# Revit family: Hager-GOLF-Flush_mounted-IP40-With_Cover-With_DIN-NoHosted-ES-es
name_source: partatom
category: Electrical Equipment
units: mm (PartAtom-declared; Revit-internal decimal feet)

## family parameters
Always vertical = Yes
Cut with Voids When Loaded = No
Maintain Annotation Orientation = No
Panel Configuration = Two Columns, Circuits Across
Part Type = Panelboard
Room Calculation Point = No
Round Connector Dimension = Use Diameter
Shared = No
Work Plane-Based = Yes

## types (69) — shared parameters
Code hager = ADD-EC000214_EU
Default Elevation = 1200 mm
EF000003 - Método de montaje = Montado empotrado (escayola)
EF000007 - Color = Blanco
EF000024 - Resistente a UV = No
EF000049 - Profundidad = 97 mm  [stored 0.318241 ft]
EF000116 - Número RAL = 9010
EF000118 - Con placa de montaje = No
EF000218 - Profundidad de instalación = 72 mm  [stored 0.23622 ft]
EF001062 - Versión de CEM = No
EF001134 - Carril DIN = Yes
EF004462 - Tipo de cierre = Otros
EF005474 - Grado de protección (IP) = IP40
EF006306 - Con candado = No
EF009212 - Versión de la cubierta = Cerrado
ETIM class code = EC000214
ETIM class name = Small distribution board
HG000001 - Número de columnas = 1
HG000002-with door or cover-es = Yes
HG000003-Range-es = GOLF
HG000005-Thickness-es = 2 mm  [stored 0.00656168 ft]
HG000006-Flush mounted-es = Yes
HG000009-Double swing door-es = No
HG000010-Asymmetric doors-es = No
HG000011-Empty rows from bottom-es = No
HG000012-Door swing angle-es = 90.00°
HG000013-Door on the left-es = No
HG000014-Door on the right-es = Yes
HG000015-Clearance visibility-es = Yes
HG000016-Door 3D visibility-es = Yes
HG000017-Distance between poles-es = 18 mm  [stored 0.0590551 ft]
HG000060-RAL-number = 9010
HG000099-Onfly Template ID-es-ES = 507532
Manufacturer = Hager
Name BIM&CO = Electricity
Name hager = ADD_Enclosures_EC000214
Reference = Template-Enclosure_EU-EC000214
Uniformat = Low Tension Service & Dist.
Uniformat code = D501001
zero-valued in all types: EF001131 - Profundidad interna, HG000007-Number of empty columns-es, HG000008-Number of empty rows-es

## per-type parameters (varying)
| type | BC_METADATA | EF000008 - Anchura | EF000040 - Altura | EF000266 - Número de filas | EF000332 - Altura de la instalación | EF000846 - Anchura de montaje | EF001088 - Posibilidad de extensión | EF002950 - Ancho en número de espacios modulares | EF006244 - Tapa/puerta transparente | EF015776 - Borne de tierra | EF015777 - Borne neutro | EF015941 - Puerta de transmisión de señal | HG000004-Manufacturer reference-es | HGEF000266-Número de filas | HGEF0002950-Ancho en número de espacios modulares |
| GOLF-Flush_mounted_W204_H225_D97_4_Modular_Spacing-VF104PE | {"ObjectGuid":"21a461f2-d2cc-43be-887c-1bcd842bd4ee","ModelGuid":"3472f7aa-0217-42d1-acd3-302686f3a51c","VariantGuid":"67abac47-0447-4a06-9074-36f65eb0749b","Revision":"#5","VariantName":"GOLF-Flush_mounted_W204_H225_D97_4_Modular_Spacing-VF104PE"} | 204 mm | 225 mm  [stored 0.738189 ft] | 1 | 189 mm  [stored 0.620079 ft] | 170 mm  [stored 0.557743 ft] | Yes | 4 | No | Yes | No | Yes | VF104PE | 1 | 4 |
| GOLF-Flush_mounted_W204_H225_D97_4_Modular_Spacing-VF104PEH | {"ObjectGuid":"21a461f2-d2cc-43be-887c-1bcd842bd4ee","ModelGuid":"3472f7aa-0217-42d1-acd3-302686f3a51c","VariantGuid":"bf5ffc28-fc6f-4c9d-8d83-cb40cf3ecd5b","Revision":"#5","VariantName":"GOLF-Flush_mounted_W204_H225_D97_4_Modular_Spacing-VF104PEH"} | 204 mm | 225 mm  [stored 0.738189 ft] | 1 | 189 mm  [stored 0.620079 ft] | 170 mm  [stored 0.557743 ft] | Yes | 4 | No | Yes | No | Yes | VF104PEH | 1 | 4 |
| GOLF-Flush_mounted_W204_H225_D97_4_Modular_Spacing-VF104TE | {"ObjectGuid":"21a461f2-d2cc-43be-887c-1bcd842bd4ee","ModelGuid":"3472f7aa-0217-42d1-acd3-302686f3a51c","VariantGuid":"7042e25b-f324-46a0-bf15-9dd9586686e8","Revision":"#5","VariantName":"GOLF-Flush_mounted_W204_H225_D97_4_Modular_Spacing-VF104TE"} | 204 mm | 225 mm  [stored 0.738189 ft] | 1 | 189 mm  [stored 0.620079 ft] | 170 mm  [stored 0.557743 ft] | Yes | 4 | Yes | Yes | No | Yes | VF104TE | 1 | 4 |
| GOLF-Flush_mounted_W275_H225_D97_8_Modular_Spacing-VF108PE | {"ObjectGuid":"21a461f2-d2cc-43be-887c-1bcd842bd4ee","ModelGuid":"3472f7aa-0217-42d1-acd3-302686f3a51c","VariantGuid":"06116414-54d7-4273-82dc-95a411ece082","Revision":"#5","VariantName":"GOLF-Flush_mounted_W275_H225_D97_8_Modular_Spacing-VF108PE"} | 275 mm | 225 mm  [stored 0.738189 ft] | 1 | 189 mm  [stored 0.620079 ft] | 242 mm  [stored 0.793963 ft] | Yes | 8 | No | Yes | No | Yes | VF108PE | 1 | 8 |
| GOLF-Flush_mounted_W275_H225_D97_8_Modular_Spacing-VF108PEH | {"ObjectGuid":"21a461f2-d2cc-43be-887c-1bcd842bd4ee","ModelGuid":"3472f7aa-0217-42d1-acd3-302686f3a51c","VariantGuid":"36ce2ec1-e60a-4bf2-a514-3e6662372eb3","Revision":"#5","VariantName":"GOLF-Flush_mounted_W275_H225_D97_8_Modular_Spacing-VF108PEH"} | 275 mm | 225 mm  [stored 0.738189 ft] | 1 | 189 mm  [stored 0.620079 ft] | 242 mm  [stored 0.793963 ft] | Yes | 8 | No | Yes | No | Yes | VF108PEH | 1 | 8 |
| GOLF-Flush_mounted_W275_H225_D97_8_Modular_Spacing-VF108TE | {"ObjectGuid":"21a461f2-d2cc-43be-887c-1bcd842bd4ee","ModelGuid":"3472f7aa-0217-42d1-acd3-302686f3a51c","VariantGuid":"5955d0a4-5d32-445a-b466-02b6bf6b212f","Revision":"#5","VariantName":"GOLF-Flush_mounted_W275_H225_D97_8_Modular_Spacing-VF108TE"} | 275 mm | 225 mm  [stored 0.738189 ft] | 1 | 189 mm  [stored 0.620079 ft] | 242 mm  [stored 0.793963 ft] | Yes | 8 | Yes | Yes | No | Yes | VF108TE | 1 | 8 |
| GOLF-Flush_mounted_W275_H225_D97_8_Modular_Spacing-VF108TJ | {"ObjectGuid":"21a461f2-d2cc-43be-887c-1bcd842bd4ee","ModelGuid":"3472f7aa-0217-42d1-acd3-302686f3a51c","VariantGuid":"db803c6c-c584-49ad-b8cc-c973fc13c8e5","Revision":"#5","VariantName":"GOLF-Flush_mounted_W275_H225_D97_8_Modular_Spacing-VF108TJ"} | 275 mm | 225 mm  [stored 0.738189 ft] | 1 | 189 mm  [stored 0.620079 ft] | 242 mm  [stored 0.793963 ft] | Yes | 8 | Yes | Yes | Yes | Yes | VF108TJ | 1 | 8 |
| GOLF-Flush_mounted_W352_H293_D97_12_Modular_Spacing-VF112PE | {"ObjectGuid":"21a461f2-d2cc-43be-887c-1bcd842bd4ee","ModelGuid":"3472f7aa-0217-42d1-acd3-302686f3a51c","VariantGuid":"c39431f9-d04a-4a2b-91f6-57de3b093784","Revision":"#5","VariantName":"GOLF-Flush_mounted_W352_H293_D97_12_Modular_Spacing-VF112PE"} | 352 mm  [stored 1.15486 ft] | 293 mm | 1 | 257 mm  [stored 0.843176 ft] | 318 mm  [stored 1.04331 ft] | Yes | 12 | No | Yes | No | Yes | VF112PE | 1 | 12 |
| GOLF-Flush_mounted_W352_H293_D97_12_Modular_Spacing-VF112PEH | {"ObjectGuid":"21a461f2-d2cc-43be-887c-1bcd842bd4ee","ModelGuid":"3472f7aa-0217-42d1-acd3-302686f3a51c","VariantGuid":"8f0d8f87-0006-4b11-8d38-30c6d8bf758f","Revision":"#5","VariantName":"GOLF-Flush_mounted_W352_H293_D97_12_Modular_Spacing-VF112PEH"} | 352 mm  [stored 1.15486 ft] | 293 mm | 1 | 257 mm  [stored 0.843176 ft] | 318 mm  [stored 1.04331 ft] | Yes | 12 | No | Yes | No | Yes | VF112PEH | 1 | 12 |
| GOLF-Flush_mounted_W352_H293_D97_12_Modular_Spacing-VF112PJ | {"ObjectGuid":"21a461f2-d2cc-43be-887c-1bcd842bd4ee","ModelGuid":"3472f7aa-0217-42d1-acd3-302686f3a51c","VariantGuid":"0c9c232a-2e7f-4892-bcb4-da88733a4bf1","Revision":"#5","VariantName":"GOLF-Flush_mounted_W352_H293_D97_12_Modular_Spacing-VF112PJ"} | 352 mm  [stored 1.15486 ft] | 293 mm | 1 | 257 mm  [stored 0.843176 ft] | 318 mm  [stored 1.04331 ft] | Yes | 12 | No | Yes | Yes | Yes | VF112PJ | 1 | 12 |
| GOLF-Flush_mounted_W352_H293_D97_12_Modular_Spacing-VF112PY | {"ObjectGuid":"21a461f2-d2cc-43be-887c-1bcd842bd4ee","ModelGuid":"3472f7aa-0217-42d1-acd3-302686f3a51c","VariantGuid":"afb2a40a-fb85-4b57-bab9-55e2ace79b82","Revision":"#5","VariantName":"GOLF-Flush_mounted_W352_H293_D97_12_Modular_Spacing-VF112PY"} | 352 mm  [stored 1.15486 ft] | 293 mm | 1 | 257 mm  [stored 0.843176 ft] | 318 mm  [stored 1.04331 ft] | Yes | 12 | No | No | No | No | VF112PY | 1 | 12 |
| GOLF-Flush_mounted_W352_H293_D97_12_Modular_Spacing-VF112TE | {"ObjectGuid":"21a461f2-d2cc-43be-887c-1bcd842bd4ee","ModelGuid":"3472f7aa-0217-42d1-acd3-302686f3a51c","VariantGuid":"56dcd90f-e5ad-4723-8c6c-981950e4aafb","Revision":"#5","VariantName":"GOLF-Flush_mounted_W352_H293_D97_12_Modular_Spacing-VF112TE"} | 352 mm  [stored 1.15486 ft] | 293 mm | 1 | 257 mm  [stored 0.843176 ft] | 318 mm  [stored 1.04331 ft] | Yes | 12 | Yes | Yes | No | Yes | VF112TE | 1 | 12 |
| GOLF-Flush_mounted_W352_H293_D97_12_Modular_Spacing-VF112TF | {"ObjectGuid":"21a461f2-d2cc-43be-887c-1bcd842bd4ee","ModelGuid":"3472f7aa-0217-42d1-acd3-302686f3a51c","VariantGuid":"18a8c72d-3909-411f-af7f-3ef0debf2d79","Revision":"#5","VariantName":"GOLF-Flush_mounted_W352_H293_D97_12_Modular_Spacing-VF112TF"} | 352 mm  [stored 1.15486 ft] | 293 mm | 1 | 257 mm  [stored 0.843176 ft] | 318 mm  [stored 1.04331 ft] | Yes | 12 | Yes | Yes | No | Yes | VF112TF | 1 | 12 |
| GOLF-Flush_mounted_W352_H293_D97_12_Modular_Spacing-VF112TJ | {"ObjectGuid":"21a461f2-d2cc-43be-887c-1bcd842bd4ee","ModelGuid":"3472f7aa-0217-42d1-acd3-302686f3a51c","VariantGuid":"e8fe70cc-cd10-46dc-9450-fec8598aad3c","Revision":"#5","VariantName":"GOLF-Flush_mounted_W352_H293_D97_12_Modular_Spacing-VF112TJ"} | 352 mm  [stored 1.15486 ft] | 293 mm | 1 | 257 mm  [stored 0.843176 ft] | 318 mm  [stored 1.04331 ft] | Yes | 12 | Yes | Yes | Yes | Yes | VF112TJ | 1 | 12 |
| GOLF-Flush_mounted_W352_H293_D97_12_Modular_Spacing-VF112TY | {"ObjectGuid":"21a461f2-d2cc-43be-887c-1bcd842bd4ee","ModelGuid":"3472f7aa-0217-42d1-acd3-302686f3a51c","VariantGuid":"f1fc716c-5d21-43a4-b735-6e5759e6688c","Revision":"#5","VariantName":"GOLF-Flush_mounted_W352_H293_D97_12_Modular_Spacing-VF112TY"} | 352 mm  [stored 1.15486 ft] | 293 mm | 1 | 257 mm  [stored 0.843176 ft] | 318 mm  [stored 1.04331 ft] | Yes | 12 | Yes | Yes | Yes | Yes | VF112TY | 1 | 12 |
| GOLF-Flush_mounted_W460_H293_D97_18_Modular_Spacing-VF118PEH | {"ObjectGuid":"21a461f2-d2cc-43be-887c-1bcd842bd4ee","ModelGuid":"3472f7aa-0217-42d1-acd3-302686f3a51c","VariantGuid":"ae20f4c4-2976-4c92-9248-da306b9a1619","Revision":"#5","VariantName":"GOLF-Flush_mounted_W460_H293_D97_18_Modular_Spacing-VF118PEH"} | 460 mm  [stored 1.50919 ft] | 293 mm | 1 | 257 mm  [stored 0.843176 ft] | 426 mm  [stored 1.39764 ft] | Yes | 18 | No | Yes | No | Yes | VF118PEH | 1 | 18 |
| GOLF-Flush_mounted_W460_H293_D97_18_Modular_Spacing-VF118PES | {"ObjectGuid":"21a461f2-d2cc-43be-887c-1bcd842bd4ee","ModelGuid":"3472f7aa-0217-42d1-acd3-302686f3a51c","VariantGuid":"5cf63521-b8ed-4543-b6dc-da1827a879bf","Revision":"#5","VariantName":"GOLF-Flush_mounted_W460_H293_D97_18_Modular_Spacing-VF118PES"} | 460 mm  [stored 1.50919 ft] | 293 mm | 1 | 257 mm  [stored 0.843176 ft] | 426 mm  [stored 1.39764 ft] | Yes | 18 | No | No | No | Yes | VF118PES | 1 | 18 |
| GOLF-Flush_mounted_W460_H293_D97_18_Modular_Spacing-VF118PJ | {"ObjectGuid":"21a461f2-d2cc-43be-887c-1bcd842bd4ee","ModelGuid":"3472f7aa-0217-42d1-acd3-302686f3a51c","VariantGuid":"8448448f-abc3-4fb3-a180-206e74746064","Revision":"#5","VariantName":"GOLF-Flush_mounted_W460_H293_D97_18_Modular_Spacing-VF118PJ"} | 460 mm  [stored 1.50919 ft] | 293 mm | 1 | 257 mm  [stored 0.843176 ft] | 426 mm  [stored 1.39764 ft] | Yes | 18 | No | Yes | Yes | Yes | VF118PJ | 1 | 18 |
| GOLF-Flush_mounted_W460_H293_D97_18_Modular_Spacing-VF118PY | {"ObjectGuid":"21a461f2-d2cc-43be-887c-1bcd842bd4ee","ModelGuid":"3472f7aa-0217-42d1-acd3-302686f3a51c","VariantGuid":"7df140ba-cf3c-4387-8973-dca42f2361fd","Revision":"#5","VariantName":"GOLF-Flush_mounted_W460_H293_D97_18_Modular_Spacing-VF118PY"} | 460 mm  [stored 1.50919 ft] | 293 mm | 1 | 257 mm  [stored 0.843176 ft] | 426 mm  [stored 1.39764 ft] | Yes | 18 | No | Yes | Yes | Yes | VF118PY | 1 | 18 |
| GOLF-Flush_mounted_W460_H293_D97_18_Modular_Spacing-VF118TES | {"ObjectGuid":"21a461f2-d2cc-43be-887c-1bcd842bd4ee","ModelGuid":"3472f7aa-0217-42d1-acd3-302686f3a51c","VariantGuid":"4f697f37-6e24-4481-bb3c-c0125da33d8b","Revision":"#5","VariantName":"GOLF-Flush_mounted_W460_H293_D97_18_Modular_Spacing-VF118TES"} | 460 mm  [stored 1.50919 ft] | 293 mm | 1 | 257 mm  [stored 0.843176 ft] | 426 mm  [stored 1.39764 ft] | Yes | 18 | Yes | No | No | Yes | VF118TES | 1 | 18 |
| GOLF-Flush_mounted_W460_H293_D97_18_Modular_Spacing-VF118TF | {"ObjectGuid":"21a461f2-d2cc-43be-887c-1bcd842bd4ee","ModelGuid":"3472f7aa-0217-42d1-acd3-302686f3a51c","VariantGuid":"ee03994c-8386-4bc1-b826-dbc84356b814","Revision":"#5","VariantName":"GOLF-Flush_mounted_W460_H293_D97_18_Modular_Spacing-VF118TF"} | 460 mm  [stored 1.50919 ft] | 293 mm | 1 | 257 mm  [stored 0.843176 ft] | 426 mm  [stored 1.39764 ft] | Yes | 18 | Yes | Yes | No | Yes | VF118TF | 1 | 18 |
| GOLF-Flush_mounted_W460_H293_D97_18_Modular_Spacing-VF118TJ | {"ObjectGuid":"21a461f2-d2cc-43be-887c-1bcd842bd4ee","ModelGuid":"3472f7aa-0217-42d1-acd3-302686f3a51c","VariantGuid":"209a2a37-a07e-4dc6-b282-929268ae2f3a","Revision":"#5","VariantName":"GOLF-Flush_mounted_W460_H293_D97_18_Modular_Spacing-VF118TJ"} | 460 mm  [stored 1.50919 ft] | 293 mm | 1 | 257 mm  [stored 0.843176 ft] | 426 mm  [stored 1.39764 ft] | Yes | 18 | Yes | Yes | Yes | Yes | VF118TJ | 1 | 18 |
| GOLF-Flush_mounted_W532_H293_D97_22_Modular_Spacing-VF122PJ | {"ObjectGuid":"21a461f2-d2cc-43be-887c-1bcd842bd4ee","ModelGuid":"3472f7aa-0217-42d1-acd3-302686f3a51c","VariantGuid":"5168d309-5bef-4431-903a-a28adc8417b0","Revision":"#5","VariantName":"GOLF-Flush_mounted_W532_H293_D97_22_Modular_Spacing-VF122PJ"} | 532 mm  [stored 1.74541 ft] | 293 mm | 1 | 257 mm  [stored 0.843176 ft] | 498 mm  [stored 1.63386 ft] | Yes | 22 | No | Yes | Yes | Yes | VF122PJ | 1 | 22 |
| GOLF-Flush_mounted_W532_H293_D97_22_Modular_Spacing-VF122PY | {"ObjectGuid":"21a461f2-d2cc-43be-887c-1bcd842bd4ee","ModelGuid":"3472f7aa-0217-42d1-acd3-302686f3a51c","VariantGuid":"328723d9-22b9-4b39-9473-d80da34b37ed","Revision":"#5","VariantName":"GOLF-Flush_mounted_W532_H293_D97_22_Modular_Spacing-VF122PY"} | 532 mm  [stored 1.74541 ft] | 293 mm | 1 | 257 mm  [stored 0.843176 ft] | 498 mm  [stored 1.63386 ft] | Yes | 22 | No | Yes | Yes | Yes | VF122PY | 1 | 22 |
| GOLF-Flush_mounted_W532_H293_D97_22_Modular_Spacing-VF122TJ | {"ObjectGuid":"21a461f2-d2cc-43be-887c-1bcd842bd4ee","ModelGuid":"3472f7aa-0217-42d1-acd3-302686f3a51c","VariantGuid":"3a9b3df3-2168-4687-926f-6f447096e5eb","Revision":"#5","VariantName":"GOLF-Flush_mounted_W532_H293_D97_22_Modular_Spacing-VF122TJ"} | 532 mm  [stored 1.74541 ft] | 293 mm | 1 | 257 mm  [stored 0.843176 ft] | 498 mm  [stored 1.63386 ft] | Yes | 22 | Yes | Yes | Yes | Yes | VF122TJ | 1 | 22 |
| GOLF-Flush_mounted_W382_H418_D97_12_Modular_Spacing-VF212PE | {"ObjectGuid":"21a461f2-d2cc-43be-887c-1bcd842bd4ee","ModelGuid":"3472f7aa-0217-42d1-acd3-302686f3a51c","VariantGuid":"1e1221e6-b138-42e7-8c4c-b4154327bed8","Revision":"#5","VariantName":"GOLF-Flush_mounted_W382_H418_D97_12_Modular_Spacing-VF212PE"} | 382 mm  [stored 1.25328 ft] | 418 mm  [stored 1.37139 ft] | 2 | 382 mm  [stored 1.25328 ft] | 318 mm  [stored 1.04331 ft] | Yes | 12 | No | Yes | No | Yes | VF212PE | 2 | 12 |
| GOLF-Flush_mounted_W382_H418_D97_12_Modular_Spacing-VF212PEH | {"ObjectGuid":"21a461f2-d2cc-43be-887c-1bcd842bd4ee","ModelGuid":"3472f7aa-0217-42d1-acd3-302686f3a51c","VariantGuid":"882bf6e7-a5db-46d6-a215-6183fbc56335","Revision":"#5","VariantName":"GOLF-Flush_mounted_W382_H418_D97_12_Modular_Spacing-VF212PEH"} | 382 mm  [stored 1.25328 ft] | 418 mm  [stored 1.37139 ft] | 2 | 382 mm  [stored 1.25328 ft] | 318 mm  [stored 1.04331 ft] | Yes | 12 | No | Yes | No | Yes | VF212PEH | 2 | 12 |
| GOLF-Flush_mounted_W382_H418_D97_12_Modular_Spacing-VF212PJ | {"ObjectGuid":"21a461f2-d2cc-43be-887c-1bcd842bd4ee","ModelGuid":"3472f7aa-0217-42d1-acd3-302686f3a51c","VariantGuid":"8b850704-ff25-4561-b558-594a17e3e1ae","Revision":"#5","VariantName":"GOLF-Flush_mounted_W382_H418_D97_12_Modular_Spacing-VF212PJ"} | 382 mm  [stored 1.25328 ft] | 418 mm  [stored 1.37139 ft] | 2 | 382 mm  [stored 1.25328 ft] | 318 mm  [stored 1.04331 ft] | Yes | 12 | No | Yes | Yes | Yes | VF212PJ | 2 | 12 |
| GOLF-Flush_mounted_W382_H418_D97_12_Modular_Spacing-VF212PY | {"ObjectGuid":"21a461f2-d2cc-43be-887c-1bcd842bd4ee","ModelGuid":"3472f7aa-0217-42d1-acd3-302686f3a51c","VariantGuid":"689b9795-30a9-4674-b1e6-8e2635905e1d","Revision":"#5","VariantName":"GOLF-Flush_mounted_W382_H418_D97_12_Modular_Spacing-VF212PY"} | 382 mm  [stored 1.25328 ft] | 418 mm  [stored 1.37139 ft] | 2 | 382 mm  [stored 1.25328 ft] | 318 mm  [stored 1.04331 ft] | Yes | 12 | No | Yes | Yes | Yes | VF212PY | 2 | 12 |
| GOLF-Flush_mounted_W382_H418_D97_12_Modular_Spacing-VF212TE | {"ObjectGuid":"21a461f2-d2cc-43be-887c-1bcd842bd4ee","ModelGuid":"3472f7aa-0217-42d1-acd3-302686f3a51c","VariantGuid":"9b9d8c79-640a-4a36-9dd2-bba10c2b1196","Revision":"#5","VariantName":"GOLF-Flush_mounted_W382_H418_D97_12_Modular_Spacing-VF212TE"} | 382 mm  [stored 1.25328 ft] | 418 mm  [stored 1.37139 ft] | 2 | 382 mm  [stored 1.25328 ft] | 318 mm  [stored 1.04331 ft] | Yes | 12 | Yes | Yes | No | Yes | VF212TE | 2 | 12 |
| GOLF-Flush_mounted_W382_H418_D97_12_Modular_Spacing-VF212TF | {"ObjectGuid":"21a461f2-d2cc-43be-887c-1bcd842bd4ee","ModelGuid":"3472f7aa-0217-42d1-acd3-302686f3a51c","VariantGuid":"26e59038-3d61-4783-9d9f-9c877d24d8f9","Revision":"#5","VariantName":"GOLF-Flush_mounted_W382_H418_D97_12_Modular_Spacing-VF212TF"} | 382 mm  [stored 1.25328 ft] | 418 mm  [stored 1.37139 ft] | 2 | 382 mm  [stored 1.25328 ft] | 318 mm  [stored 1.04331 ft] | Yes | 12 | Yes | Yes | No | Yes | VF212TF | 2 | 12 |
| GOLF-Flush_mounted_W382_H418_D97_12_Modular_Spacing-VF212TJ | {"ObjectGuid":"21a461f2-d2cc-43be-887c-1bcd842bd4ee","ModelGuid":"3472f7aa-0217-42d1-acd3-302686f3a51c","VariantGuid":"b8adb583-5659-4b02-a708-5acbf8c85fbc","Revision":"#5","VariantName":"GOLF-Flush_mounted_W382_H418_D97_12_Modular_Spacing-VF212TJ"} | 382 mm  [stored 1.25328 ft] | 418 mm  [stored 1.37139 ft] | 2 | 382 mm  [stored 1.25328 ft] | 318 mm  [stored 1.04331 ft] | Yes | 12 | Yes | Yes | Yes | Yes | VF212TJ | 2 | 12 |
| GOLF-Flush_mounted_W382_H418_D97_12_Modular_Spacing-VF212TY | {"ObjectGuid":"21a461f2-d2cc-43be-887c-1bcd842bd4ee","ModelGuid":"3472f7aa-0217-42d1-acd3-302686f3a51c","VariantGuid":"80280981-1c18-4773-a3eb-3c4e30698d3e","Revision":"#5","VariantName":"GOLF-Flush_mounted_W382_H418_D97_12_Modular_Spacing-VF212TY"} | 382 mm  [stored 1.25328 ft] | 418 mm  [stored 1.37139 ft] | 2 | 382 mm  [stored 1.25328 ft] | 318 mm  [stored 1.04331 ft] | Yes | 12 | Yes | Yes | Yes | Yes | VF212TY | 2 | 12 |
| GOLF-Flush_mounted_W460_H418_D97_18_Modular_Spacing-VF218PEH | {"ObjectGuid":"21a461f2-d2cc-43be-887c-1bcd842bd4ee","ModelGuid":"3472f7aa-0217-42d1-acd3-302686f3a51c","VariantGuid":"341dbc47-b668-45d4-978c-80e70d0aa2b6","Revision":"#5","VariantName":"GOLF-Flush_mounted_W460_H418_D97_18_Modular_Spacing-VF218PEH"} | 460 mm  [stored 1.50919 ft] | 418 mm  [stored 1.37139 ft] | 2 | 382 mm  [stored 1.25328 ft] | 426 mm  [stored 1.39764 ft] | Yes | 18 | No | Yes | No | Yes | VF218PEH | 2 | 18 |
| GOLF-Flush_mounted_W460_H418_D97_18_Modular_Spacing-VF218PES | {"ObjectGuid":"21a461f2-d2cc-43be-887c-1bcd842bd4ee","ModelGuid":"3472f7aa-0217-42d1-acd3-302686f3a51c","VariantGuid":"e95bd323-1111-4a2d-a4d2-bf3c78e84609","Revision":"#5","VariantName":"GOLF-Flush_mounted_W460_H418_D97_18_Modular_Spacing-VF218PES"} | 460 mm  [stored 1.50919 ft] | 418 mm  [stored 1.37139 ft] | 2 | 382 mm  [stored 1.25328 ft] | 426 mm  [stored 1.39764 ft] | Yes | 18 | No | No | No | Yes | VF218PES | 2 | 18 |
| GOLF-Flush_mounted_W460_H418_D97_18_Modular_Spacing-VF218PF | {"ObjectGuid":"21a461f2-d2cc-43be-887c-1bcd842bd4ee","ModelGuid":"3472f7aa-0217-42d1-acd3-302686f3a51c","VariantGuid":"c3808366-c01d-4ebf-b1de-7656891a9cc5","Revision":"#5","VariantName":"GOLF-Flush_mounted_W460_H418_D97_18_Modular_Spacing-VF218PF"} | 460 mm  [stored 1.50919 ft] | 418 mm  [stored 1.37139 ft] | 2 | 382 mm  [stored 1.25328 ft] | 426 mm  [stored 1.39764 ft] | Yes | 18 | No | Yes | No | Yes | VF218PF | 2 | 18 |
| GOLF-Flush_mounted_W460_H418_D97_18_Modular_Spacing-VF218PJ | {"ObjectGuid":"21a461f2-d2cc-43be-887c-1bcd842bd4ee","ModelGuid":"3472f7aa-0217-42d1-acd3-302686f3a51c","VariantGuid":"3d0fdefe-7e59-4817-bd97-63dfef6b0556","Revision":"#5","VariantName":"GOLF-Flush_mounted_W460_H418_D97_18_Modular_Spacing-VF218PJ"} | 460 mm  [stored 1.50919 ft] | 418 mm  [stored 1.37139 ft] | 2 | 382 mm  [stored 1.25328 ft] | 426 mm  [stored 1.39764 ft] | Yes | 18 | No | Yes | Yes | Yes | VF218PJ | 2 | 18 |
| GOLF-Flush_mounted_W460_H418_D97_18_Modular_Spacing-VF218PY | {"ObjectGuid":"21a461f2-d2cc-43be-887c-1bcd842bd4ee","ModelGuid":"3472f7aa-0217-42d1-acd3-302686f3a51c","VariantGuid":"8bb62a64-7565-4ac7-a41a-9a54e64cd793","Revision":"#5","VariantName":"GOLF-Flush_mounted_W460_H418_D97_18_Modular_Spacing-VF218PY"} | 460 mm  [stored 1.50919 ft] | 418 mm  [stored 1.37139 ft] | 2 | 382 mm  [stored 1.25328 ft] | 426 mm  [stored 1.39764 ft] | Yes | 18 | No | Yes | Yes | Yes | VF218PY | 2 | 18 |
| GOLF-Flush_mounted_W460_H418_D97_18_Modular_Spacing-VF218TES | {"ObjectGuid":"21a461f2-d2cc-43be-887c-1bcd842bd4ee","ModelGuid":"3472f7aa-0217-42d1-acd3-302686f3a51c","VariantGuid":"7211424d-8d48-41ec-a688-a34317bb0642","Revision":"#5","VariantName":"GOLF-Flush_mounted_W460_H418_D97_18_Modular_Spacing-VF218TES"} | 460 mm  [stored 1.50919 ft] | 418 mm  [stored 1.37139 ft] | 2 | 382 mm  [stored 1.25328 ft] | 426 mm  [stored 1.39764 ft] | Yes | 18 | Yes | No | No | Yes | VF218TES | 2 | 18 |
| GOLF-Flush_mounted_W460_H418_D97_18_Modular_Spacing-VF218TF | {"ObjectGuid":"21a461f2-d2cc-43be-887c-1bcd842bd4ee","ModelGuid":"3472f7aa-0217-42d1-acd3-302686f3a51c","VariantGuid":"78ee37cf-0500-43c6-a3a3-0d68ad998186","Revision":"#5","VariantName":"GOLF-Flush_mounted_W460_H418_D97_18_Modular_Spacing-VF218TF"} | 460 mm  [stored 1.50919 ft] | 418 mm  [stored 1.37139 ft] | 2 | 382 mm  [stored 1.25328 ft] | 426 mm  [stored 1.39764 ft] | No | 18 | No | No | No | No | VF218TF | 2 | 18 |
| GOLF-Flush_mounted_W460_H418_D97_18_Modular_Spacing-VF218TJ | {"ObjectGuid":"21a461f2-d2cc-43be-887c-1bcd842bd4ee","ModelGuid":"3472f7aa-0217-42d1-acd3-302686f3a51c","VariantGuid":"b4a76b88-0e50-4808-ae2c-8f31bc576c3e","Revision":"#5","VariantName":"GOLF-Flush_mounted_W460_H418_D97_18_Modular_Spacing-VF218TJ"} | 460 mm  [stored 1.50919 ft] | 418 mm  [stored 1.37139 ft] | 2 | 382 mm  [stored 1.25328 ft] | 426 mm  [stored 1.39764 ft] | Yes | 18 | Yes | Yes | Yes | Yes | VF218TJ | 2 | 18 |
| GOLF-Flush_mounted_W352_H543_D97_12_Modular_Spacing-VF312ICT | {"ObjectGuid":"21a461f2-d2cc-43be-887c-1bcd842bd4ee","ModelGuid":"3472f7aa-0217-42d1-acd3-302686f3a51c","VariantGuid":"06157bb0-7800-43fd-b967-c28e3228a739","Revision":"#5","VariantName":"GOLF-Flush_mounted_W352_H543_D97_12_Modular_Spacing-VF312ICT"} | 352 mm  [stored 1.15486 ft] | 543 mm  [stored 1.7815 ft] | 3 | 507 mm  [stored 1.66339 ft] | 318 mm  [stored 1.04331 ft] | Yes | 12 | No | No | No | Yes | VF312ICT | 3 | 12 |
| GOLF-Flush_mounted_W352_H543_D97_12_Modular_Spacing-VF312PE | {"ObjectGuid":"21a461f2-d2cc-43be-887c-1bcd842bd4ee","ModelGuid":"3472f7aa-0217-42d1-acd3-302686f3a51c","VariantGuid":"683d2f02-b507-4480-903c-6f8901663eb9","Revision":"#5","VariantName":"GOLF-Flush_mounted_W352_H543_D97_12_Modular_Spacing-VF312PE"} | 352 mm  [stored 1.15486 ft] | 543 mm  [stored 1.7815 ft] | 3 | 507 mm  [stored 1.66339 ft] | 318 mm  [stored 1.04331 ft] | Yes | 12 | No | Yes | No | Yes | VF312PE | 3 | 12 |
| GOLF-Flush_mounted_W352_H543_D97_12_Modular_Spacing-VF312PEH | {"ObjectGuid":"21a461f2-d2cc-43be-887c-1bcd842bd4ee","ModelGuid":"3472f7aa-0217-42d1-acd3-302686f3a51c","VariantGuid":"913ba4ed-7dee-49ff-980f-86187e50a59b","Revision":"#5","VariantName":"GOLF-Flush_mounted_W352_H543_D97_12_Modular_Spacing-VF312PEH"} | 352 mm  [stored 1.15486 ft] | 543 mm  [stored 1.7815 ft] | 3 | 507 mm  [stored 1.66339 ft] | 318 mm  [stored 1.04331 ft] | Yes | 12 | No | Yes | No | Yes | VF312PEH | 3 | 12 |
| GOLF-Flush_mounted_W352_H543_D97_12_Modular_Spacing-VF312PJ | {"ObjectGuid":"21a461f2-d2cc-43be-887c-1bcd842bd4ee","ModelGuid":"3472f7aa-0217-42d1-acd3-302686f3a51c","VariantGuid":"5892689f-b8d4-4707-a18d-046cf619b502","Revision":"#5","VariantName":"GOLF-Flush_mounted_W352_H543_D97_12_Modular_Spacing-VF312PJ"} | 352 mm  [stored 1.15486 ft] | 543 mm  [stored 1.7815 ft] | 3 | 507 mm  [stored 1.66339 ft] | 318 mm  [stored 1.04331 ft] | Yes | 12 | No | Yes | Yes | Yes | VF312PJ | 3 | 12 |
| GOLF-Flush_mounted_W352_H543_D97_12_Modular_Spacing-VF312PY | {"ObjectGuid":"21a461f2-d2cc-43be-887c-1bcd842bd4ee","ModelGuid":"3472f7aa-0217-42d1-acd3-302686f3a51c","VariantGuid":"9b2659e5-b158-462e-a5b1-884fc84cc13e","Revision":"#5","VariantName":"GOLF-Flush_mounted_W352_H543_D97_12_Modular_Spacing-VF312PY"} | 352 mm  [stored 1.15486 ft] | 543 mm  [stored 1.7815 ft] | 3 | 507 mm  [stored 1.66339 ft] | 318 mm  [stored 1.04331 ft] | Yes | 12 | No | Yes | Yes | Yes | VF312PY | 3 | 12 |
| GOLF-Flush_mounted_W352_H543_D97_12_Modular_Spacing-VF312TE | {"ObjectGuid":"21a461f2-d2cc-43be-887c-1bcd842bd4ee","ModelGuid":"3472f7aa-0217-42d1-acd3-302686f3a51c","VariantGuid":"897115d4-ee80-4c49-9ec2-776791fbe858","Revision":"#5","VariantName":"GOLF-Flush_mounted_W352_H543_D97_12_Modular_Spacing-VF312TE"} | 352 mm  [stored 1.15486 ft] | 543 mm  [stored 1.7815 ft] | 3 | 507 mm  [stored 1.66339 ft] | 318 mm  [stored 1.04331 ft] | Yes | 12 | Yes | Yes | No | Yes | VF312TE | 3 | 12 |
| GOLF-Flush_mounted_W352_H543_D97_12_Modular_Spacing-VF312TF | {"ObjectGuid":"21a461f2-d2cc-43be-887c-1bcd842bd4ee","ModelGuid":"3472f7aa-0217-42d1-acd3-302686f3a51c","VariantGuid":"d81e7af3-8c9b-4e12-a6f7-03cd40dfaf7b","Revision":"#5","VariantName":"GOLF-Flush_mounted_W352_H543_D97_12_Modular_Spacing-VF312TF"} | 352 mm  [stored 1.15486 ft] | 543 mm  [stored 1.7815 ft] | 3 | 507 mm  [stored 1.66339 ft] | 318 mm  [stored 1.04331 ft] | Yes | 12 | Yes | Yes | No | Yes | VF312TF | 3 | 12 |
| GOLF-Flush_mounted_W352_H543_D97_12_Modular_Spacing-VF312TJ | {"ObjectGuid":"21a461f2-d2cc-43be-887c-1bcd842bd4ee","ModelGuid":"3472f7aa-0217-42d1-acd3-302686f3a51c","VariantGuid":"ed9d222a-a38a-4a3c-be6a-f7942e6614c8","Revision":"#5","VariantName":"GOLF-Flush_mounted_W352_H543_D97_12_Modular_Spacing-VF312TJ"} | 352 mm  [stored 1.15486 ft] | 543 mm  [stored 1.7815 ft] | 3 | 507 mm  [stored 1.66339 ft] | 318 mm  [stored 1.04331 ft] | Yes | 12 | Yes | Yes | Yes | Yes | VF312TJ | 3 | 12 |
| GOLF-Flush_mounted_W352_H543_D97_12_Modular_Spacing-VF312TY | {"ObjectGuid":"21a461f2-d2cc-43be-887c-1bcd842bd4ee","ModelGuid":"3472f7aa-0217-42d1-acd3-302686f3a51c","VariantGuid":"4065c120-be1f-4f97-9c11-85e7f9010a63","Revision":"#5","VariantName":"GOLF-Flush_mounted_W352_H543_D97_12_Modular_Spacing-VF312TY"} | 352 mm  [stored 1.15486 ft] | 543 mm  [stored 1.7815 ft] | 3 | 507 mm  [stored 1.66339 ft] | 318 mm  [stored 1.04331 ft] | Yes | 12 | Yes | Yes | Yes | Yes | VF312TY | 3 | 12 |
| GOLF-Flush_mounted_W460_H543_D97_18_Modular_Spacing-VF318PEH | {"ObjectGuid":"21a461f2-d2cc-43be-887c-1bcd842bd4ee","ModelGuid":"3472f7aa-0217-42d1-acd3-302686f3a51c","VariantGuid":"e859f500-05c0-40e4-999b-1a65c3b047e4","Revision":"#5","VariantName":"GOLF-Flush_mounted_W460_H543_D97_18_Modular_Spacing-VF318PEH"} | 460 mm  [stored 1.50919 ft] | 543 mm  [stored 1.7815 ft] | 3 | 507 mm  [stored 1.66339 ft] | 426 mm  [stored 1.39764 ft] | Yes | 18 | No | Yes | No | Yes | VF318PEH | 3 | 18 |
| GOLF-Flush_mounted_W460_H543_D97_18_Modular_Spacing-VF318PES | {"ObjectGuid":"21a461f2-d2cc-43be-887c-1bcd842bd4ee","ModelGuid":"3472f7aa-0217-42d1-acd3-302686f3a51c","VariantGuid":"909e0494-e85d-4594-9e2c-44bc826086f8","Revision":"#5","VariantName":"GOLF-Flush_mounted_W460_H543_D97_18_Modular_Spacing-VF318PES"} | 460 mm  [stored 1.50919 ft] | 543 mm  [stored 1.7815 ft] | 3 | 507 mm  [stored 1.66339 ft] | 426 mm  [stored 1.39764 ft] | Yes | 18 | No | No | No | Yes | VF318PES | 3 | 18 |
| GOLF-Flush_mounted_W460_H543_D97_18_Modular_Spacing-VF318PJ | {"ObjectGuid":"21a461f2-d2cc-43be-887c-1bcd842bd4ee","ModelGuid":"3472f7aa-0217-42d1-acd3-302686f3a51c","VariantGuid":"da8285dd-d232-48f5-920c-830c71461449","Revision":"#5","VariantName":"GOLF-Flush_mounted_W460_H543_D97_18_Modular_Spacing-VF318PJ"} | 460 mm  [stored 1.50919 ft] | 543 mm  [stored 1.7815 ft] | 3 | 507 mm  [stored 1.66339 ft] | 426 mm  [stored 1.39764 ft] | Yes | 18 | No | Yes | Yes | Yes | VF318PJ | 3 | 18 |
| GOLF-Flush_mounted_W460_H543_D97_18_Modular_Spacing-VF318PY | {"ObjectGuid":"21a461f2-d2cc-43be-887c-1bcd842bd4ee","ModelGuid":"3472f7aa-0217-42d1-acd3-302686f3a51c","VariantGuid":"e2605458-ebef-44a5-b5f8-42c3d193f389","Revision":"#5","VariantName":"GOLF-Flush_mounted_W460_H543_D97_18_Modular_Spacing-VF318PY"} | 460 mm  [stored 1.50919 ft] | 543 mm  [stored 1.7815 ft] | 3 | 507 mm  [stored 1.66339 ft] | 426 mm  [stored 1.39764 ft] | Yes | 18 | No | Yes | Yes | Yes | VF318PY | 3 | 18 |
| GOLF-Flush_mounted_W460_H543_D97_18_Modular_Spacing-VF318TES | {"ObjectGuid":"21a461f2-d2cc-43be-887c-1bcd842bd4ee","ModelGuid":"3472f7aa-0217-42d1-acd3-302686f3a51c","VariantGuid":"d0da4aab-9933-4c5d-9690-b5890a196bd0","Revision":"#5","VariantName":"GOLF-Flush_mounted_W460_H543_D97_18_Modular_Spacing-VF318TES"} | 460 mm  [stored 1.50919 ft] | 543 mm  [stored 1.7815 ft] | 3 | 507 mm  [stored 1.66339 ft] | 426 mm  [stored 1.39764 ft] | Yes | 18 | Yes | No | No | Yes | VF318TES | 3 | 18 |
| GOLF-Flush_mounted_W460_H543_D97_18_Modular_Spacing-VF318TJ | {"ObjectGuid":"21a461f2-d2cc-43be-887c-1bcd842bd4ee","ModelGuid":"3472f7aa-0217-42d1-acd3-302686f3a51c","VariantGuid":"2ff9428d-7824-4b8d-a8ea-d83e628b6b76","Revision":"#5","VariantName":"GOLF-Flush_mounted_W460_H543_D97_18_Modular_Spacing-VF318TJ"} | 460 mm  [stored 1.50919 ft] | 543 mm  [stored 1.7815 ft] | 3 | 507 mm  [stored 1.66339 ft] | 426 mm  [stored 1.39764 ft] | Yes | 18 | Yes | Yes | Yes | Yes | VF318TJ | 3 | 18 |
| GOLF-Flush_mounted_W352_H688_D97_12_Modular_Spacing-VF412PE | {"ObjectGuid":"21a461f2-d2cc-43be-887c-1bcd842bd4ee","ModelGuid":"3472f7aa-0217-42d1-acd3-302686f3a51c","VariantGuid":"a13221ac-7638-4b6b-b49b-40bb68fcfd58","Revision":"#5","VariantName":"GOLF-Flush_mounted_W352_H688_D97_12_Modular_Spacing-VF412PE"} | 352 mm  [stored 1.15486 ft] | 688 mm  [stored 2.25722 ft] | 4 | 652 mm  [stored 2.13911 ft] | 318 mm  [stored 1.04331 ft] | Yes | 12 | No | Yes | No | Yes | VF412PE | 4 | 12 |
| GOLF-Flush_mounted_W352_H688_D97_12_Modular_Spacing-VF412PEH | {"ObjectGuid":"21a461f2-d2cc-43be-887c-1bcd842bd4ee","ModelGuid":"3472f7aa-0217-42d1-acd3-302686f3a51c","VariantGuid":"4a95ef5e-54f0-4cd4-9ed2-861514ba71c1","Revision":"#5","VariantName":"GOLF-Flush_mounted_W352_H688_D97_12_Modular_Spacing-VF412PEH"} | 352 mm  [stored 1.15486 ft] | 688 mm  [stored 2.25722 ft] | 4 | 652 mm  [stored 2.13911 ft] | 318 mm  [stored 1.04331 ft] | Yes | 12 | No | Yes | No | Yes | VF412PEH | 4 | 12 |
| GOLF-Flush_mounted_W352_H688_D97_12_Modular_Spacing-VF412PJ | {"ObjectGuid":"21a461f2-d2cc-43be-887c-1bcd842bd4ee","ModelGuid":"3472f7aa-0217-42d1-acd3-302686f3a51c","VariantGuid":"f2388a9f-979e-4afc-a410-063f6f779a77","Revision":"#5","VariantName":"GOLF-Flush_mounted_W352_H688_D97_12_Modular_Spacing-VF412PJ"} | 352 mm  [stored 1.15486 ft] | 688 mm  [stored 2.25722 ft] | 4 | 652 mm  [stored 2.13911 ft] | 318 mm  [stored 1.04331 ft] | Yes | 12 | No | Yes | Yes | Yes | VF412PJ | 4 | 12 |
| GOLF-Flush_mounted_W352_H688_D97_12_Modular_Spacing-VF412PY | {"ObjectGuid":"21a461f2-d2cc-43be-887c-1bcd842bd4ee","ModelGuid":"3472f7aa-0217-42d1-acd3-302686f3a51c","VariantGuid":"b5c8137e-5299-429f-bd97-1309c2a30063","Revision":"#5","VariantName":"GOLF-Flush_mounted_W352_H688_D97_12_Modular_Spacing-VF412PY"} | 352 mm  [stored 1.15486 ft] | 688 mm  [stored 2.25722 ft] | 4 | 652 mm  [stored 2.13911 ft] | 318 mm  [stored 1.04331 ft] | Yes | 12 | No | Yes | Yes | Yes | VF412PY | 4 | 12 |
| GOLF-Flush_mounted_W352_H688_D97_12_Modular_Spacing-VF412TE | {"ObjectGuid":"21a461f2-d2cc-43be-887c-1bcd842bd4ee","ModelGuid":"3472f7aa-0217-42d1-acd3-302686f3a51c","VariantGuid":"e641c62a-36f2-4ebb-97ad-9049264b911f","Revision":"#5","VariantName":"GOLF-Flush_mounted_W352_H688_D97_12_Modular_Spacing-VF412TE"} | 352 mm  [stored 1.15486 ft] | 688 mm  [stored 2.25722 ft] | 4 | 652 mm  [stored 2.13911 ft] | 318 mm  [stored 1.04331 ft] | Yes | 12 | Yes | Yes | No | Yes | VF412TE | 4 | 12 |
| GOLF-Flush_mounted_W352_H688_D97_12_Modular_Spacing-VF412TJ | {"ObjectGuid":"21a461f2-d2cc-43be-887c-1bcd842bd4ee","ModelGuid":"3472f7aa-0217-42d1-acd3-302686f3a51c","VariantGuid":"252232a4-a017-4259-af2e-a736846177cf","Revision":"#5","VariantName":"GOLF-Flush_mounted_W352_H688_D97_12_Modular_Spacing-VF412TJ"} | 352 mm  [stored 1.15486 ft] | 688 mm  [stored 2.25722 ft] | 4 | 652 mm  [stored 2.13911 ft] | 318 mm  [stored 1.04331 ft] | Yes | 12 | Yes | Yes | Yes | Yes | VF412TJ | 4 | 12 |
| GOLF-Flush_mounted_W460_H688_D97_18_Modular_Spacing-VF418PEH | {"ObjectGuid":"21a461f2-d2cc-43be-887c-1bcd842bd4ee","ModelGuid":"3472f7aa-0217-42d1-acd3-302686f3a51c","VariantGuid":"8bb7e845-8ec2-4b0f-bef4-ec1a44b70135","Revision":"#5","VariantName":"GOLF-Flush_mounted_W460_H688_D97_18_Modular_Spacing-VF418PEH"} | 460 mm  [stored 1.50919 ft] | 688 mm  [stored 2.25722 ft] | 4 | 652 mm  [stored 2.13911 ft] | 426 mm  [stored 1.39764 ft] | Yes | 18 | No | Yes | No | Yes | VF418PEH | 4 | 18 |
| GOLF-Flush_mounted_W460_H688_D97_18_Modular_Spacing-VF418PES | {"ObjectGuid":"21a461f2-d2cc-43be-887c-1bcd842bd4ee","ModelGuid":"3472f7aa-0217-42d1-acd3-302686f3a51c","VariantGuid":"0932d150-7712-4254-9831-670b79f6a064","Revision":"#5","VariantName":"GOLF-Flush_mounted_W460_H688_D97_18_Modular_Spacing-VF418PES"} | 460 mm  [stored 1.50919 ft] | 688 mm  [stored 2.25722 ft] | 4 | 652 mm  [stored 2.13911 ft] | 426 mm  [stored 1.39764 ft] | Yes | 18 | No | No | No | Yes | VF418PES | 4 | 18 |
| GOLF-Flush_mounted_W460_H688_D97_18_Modular_Spacing-VF418PJ | {"ObjectGuid":"21a461f2-d2cc-43be-887c-1bcd842bd4ee","ModelGuid":"3472f7aa-0217-42d1-acd3-302686f3a51c","VariantGuid":"9ee51740-1059-4510-ae72-779836d6f5f3","Revision":"#5","VariantName":"GOLF-Flush_mounted_W460_H688_D97_18_Modular_Spacing-VF418PJ"} | 460 mm  [stored 1.50919 ft] | 688 mm  [stored 2.25722 ft] | 4 | 652 mm  [stored 2.13911 ft] | 426 mm  [stored 1.39764 ft] | Yes | 18 | No | Yes | Yes | Yes | VF418PJ | 4 | 18 |
| GOLF-Flush_mounted_W460_H688_D97_18_Modular_Spacing-VF418PY | {"ObjectGuid":"21a461f2-d2cc-43be-887c-1bcd842bd4ee","ModelGuid":"3472f7aa-0217-42d1-acd3-302686f3a51c","VariantGuid":"f0ffe918-9cda-438c-b55d-c290374f55d5","Revision":"#5","VariantName":"GOLF-Flush_mounted_W460_H688_D97_18_Modular_Spacing-VF418PY"} | 460 mm  [stored 1.50919 ft] | 688 mm  [stored 2.25722 ft] | 4 | 652 mm  [stored 2.13911 ft] | 426 mm  [stored 1.39764 ft] | Yes | 18 | No | Yes | Yes | Yes | VF418PY | 4 | 18 |
| GOLF-Flush_mounted_W460_H688_D97_18_Modular_Spacing-VF418TES | {"ObjectGuid":"21a461f2-d2cc-43be-887c-1bcd842bd4ee","ModelGuid":"3472f7aa-0217-42d1-acd3-302686f3a51c","VariantGuid":"448ad232-797f-48a6-8572-b22184c1d93f","Revision":"#5","VariantName":"GOLF-Flush_mounted_W460_H688_D97_18_Modular_Spacing-VF418TES"} | 460 mm  [stored 1.50919 ft] | 688 mm  [stored 2.25722 ft] | 4 | 652 mm  [stored 2.13911 ft] | 426 mm  [stored 1.39764 ft] | Yes | 18 | Yes | No | No | Yes | VF418TES | 4 | 18 |
| GOLF-Flush_mounted_W460_H688_D97_18_Modular_Spacing-VF418TF | {"ObjectGuid":"21a461f2-d2cc-43be-887c-1bcd842bd4ee","ModelGuid":"3472f7aa-0217-42d1-acd3-302686f3a51c","VariantGuid":"e56ca817-6faa-4ff0-9dd7-1a698eef0de9","Revision":"#5","VariantName":"GOLF-Flush_mounted_W460_H688_D97_18_Modular_Spacing-VF418TF"} | 460 mm  [stored 1.50919 ft] | 688 mm  [stored 2.25722 ft] | 4 | 652 mm  [stored 2.13911 ft] | 426 mm  [stored 1.39764 ft] | Yes | 18 | Yes | Yes | No | Yes | VF418TF | 4 | 18 |
| GOLF-Flush_mounted_W460_H688_D97_18_Modular_Spacing-VF418TJ | {"ObjectGuid":"21a461f2-d2cc-43be-887c-1bcd842bd4ee","ModelGuid":"3472f7aa-0217-42d1-acd3-302686f3a51c","VariantGuid":"b1bf4c82-785c-43f0-9c16-6322f5642611","Revision":"#5","VariantName":"GOLF-Flush_mounted_W460_H688_D97_18_Modular_Spacing-VF418TJ"} | 460 mm  [stored 1.50919 ft] | 688 mm  [stored 2.25722 ft] | 4 | 652 mm  [stored 2.13911 ft] | 426 mm  [stored 1.39764 ft] | Yes | 18 | Yes | Yes | Yes | Yes | VF418TJ | 4 | 18 |

note: [stored X ft] marks values corroborated as IEEE doubles in the binary element streams (Revit-internal decimal feet)

## geometry (parser evidence)
native form markers: Sweep x14
no freeform markers — native parametric forms only
